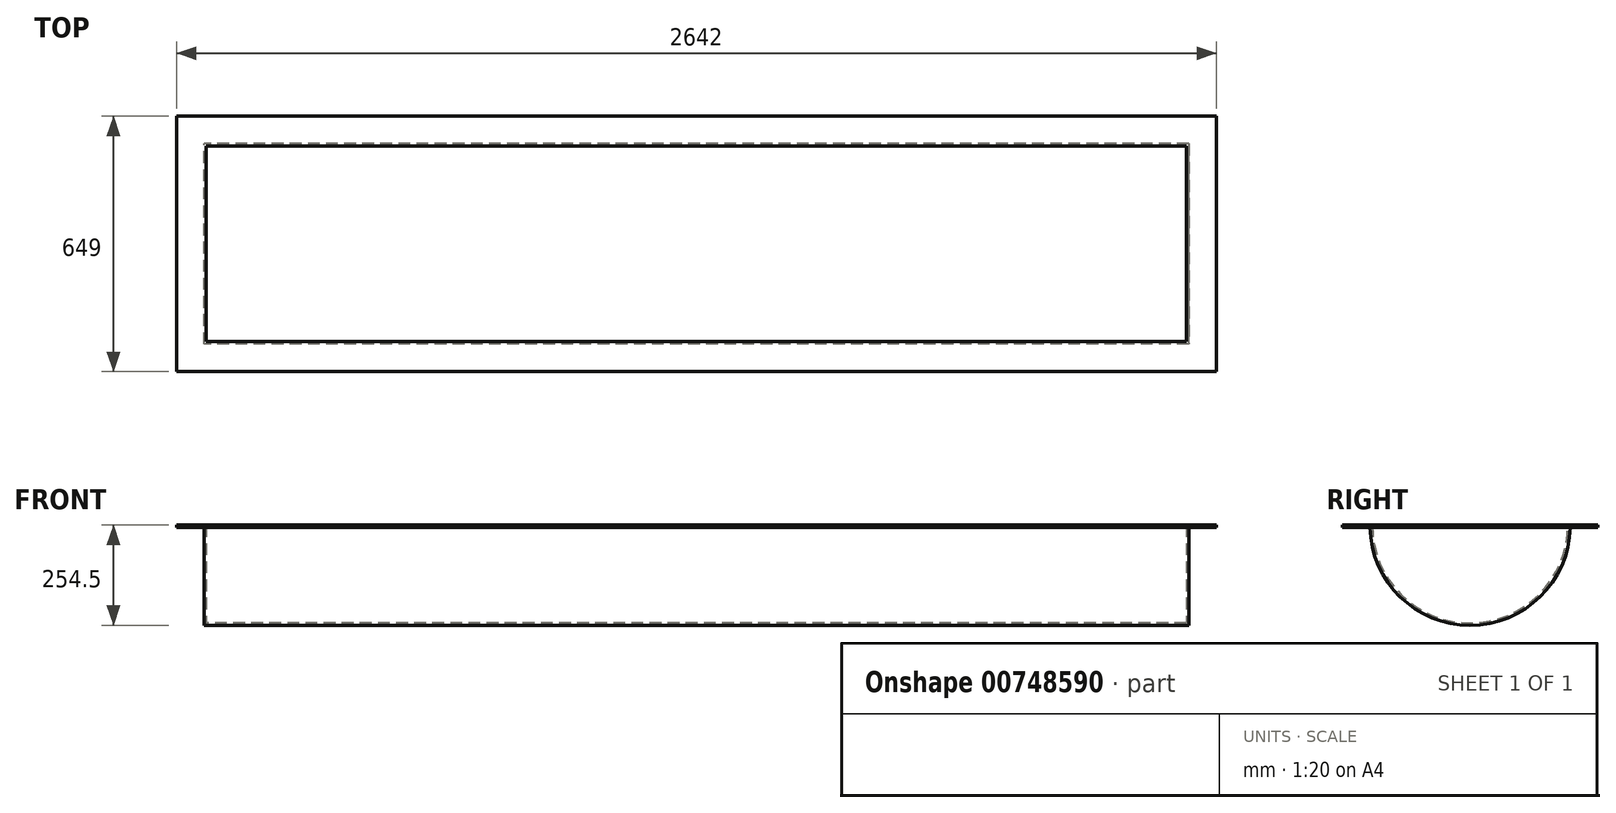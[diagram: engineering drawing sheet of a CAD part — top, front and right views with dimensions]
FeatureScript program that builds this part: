
annotation { "Feature Type Name" : "Feature", "Feature Type Description" : "" }
export const myFeature = defineFeature(function(context is Context, id is Id, definition is map)
    precondition{}
    {
        {
            var Q0;
            Q0=qCreatedBy(makeId("Right.planeOp"),FACE);
            var sketch = newSketch(context, id + "F0", { "sketchPlane" : qUnion([Q0])});
            skArc(sketch, "E0", {"start": v(-248.5, 0) * mm, "mid": v(0, -248.5) * mm, "end": v(248.5, 0) * mm});
            skArc(sketch, "E1", {"start": v(-254.5, 0) * mm, "mid": v(0, -254.5) * mm, "end": v(254.5, 0) * mm});
            skLineSegment(sketch, "E2", {"start": v(-254.5, 0) * mm, "end": v(-248.5, 0) * mm});
            skLineSegment(sketch, "E3", {"start": v(248.5, 0) * mm, "end": v(254.5, 0) * mm});
            skSolve(sketch);
        }
        {
            var Q0;
            Q0 = qSketchRegion(id + "F0", true);
            extrude(context, id + "F1", {"entities" : qUnion([Q0]), "endBound" : BoundingType.SYMMETRIC, "depth" : (2502 - 12) * mm, "offsetDistance" : 25 * mm});
        }
        {
            var Q0;
            Q0=makeQuery(id+"F1.opExtrude","CAP_FACE",FACE,{"disambiguationData":[OSD([sQuery(id+"F0.wireOp",EDGE,"E0"),sQuery(id+"F0.wireOp",EDGE,"E1"),sQuery(id+"F0.wireOp",EDGE,"E2"),sQuery(id+"F0.wireOp",EDGE,"E3")])],"isStart":false});
            var sketch = newSketch(context, id + "F2", { "sketchPlane" : qUnion([Q0])});
            skLineSegment(sketch, "E4", {"start": v(-254.5, 0) * mm, "end": v(254.5, 0) * mm});
            skArc(sketch, "E5.0", {"start": v(-254.5, 0) * mm, "mid": v(0, -254.5) * mm, "end": v(254.5, 0) * mm});
            skSolve(sketch);
        }
        {
            var Q0;
            Q0 = qSketchRegion(id + "F2", true);
            extrude(context, id + "F3", {"entities" : qUnion([Q0]), "operationType" : NewBodyOperationType.ADD, "depth" : 6 * mm, "offsetDistance" : 25 * mm});
        }
        {
            var Q0;
            Q0=makeQuery(id+"F1.opExtrude","SWEPT_BODY",BODY,{"disambiguationData":[OSD([sQuery(id+"F0.wireOp",EDGE,"E0"),sQuery(id+"F0.wireOp",EDGE,"E1"),sQuery(id+"F0.wireOp",EDGE,"E2"),sQuery(id+"F0.wireOp",EDGE,"E3")])]});
            var Q1;
            Q1=qCreatedBy(makeId("Right.planeOp"),FACE);
            mirror(context, id + "F4", {"operationType" : NewBodyOperationType.ADD, "entities" : qUnion([Q0]), "mirrorPlane" : qUnion([Q1])});
        }
        {
            var Q0;
            Q0=qCreatedBy(makeId("Top.planeOp"),FACE);
            var sketch = newSketch(context, id + "F5", { "sketchPlane" : qUnion([Q0])});
            skLineSegment(sketch, "E6.bottom", {"start": v(-1321, 324.5) * mm, "end": v(1321, 324.5) * mm});
            skLineSegment(sketch, "E6.top", {"start": v(-1321, -324.5) * mm, "end": v(1321, -324.5) * mm});
            skLineSegment(sketch, "E6.left", {"start": v(-1321, 324.5) * mm, "end": v(-1321, -324.5) * mm});
            skLineSegment(sketch, "E6.right", {"start": v(1321, 324.5) * mm, "end": v(1321, -324.5) * mm});
            skLineSegment(sketch, "E7", {"start": v(-1321, 324.5) * mm, "end": v(1321, -324.5) * mm, "construction": true});
            skSolve(sketch);
        }
        {
            var Q0;
            Q0 = qSketchRegion(id + "F5", true);
            extrude(context, id + "F6", {"entities" : qUnion([Q0]), "operationType" : NewBodyOperationType.ADD, "oppositeDirection" : true, "depth" : 6 * mm, "offsetDistance" : 25 * mm});
        }
        {
            var Q0;
            Q0=qCreatedBy(makeId("Right.planeOp"),FACE);
            var sketch = newSketch(context, id + "F7", { "sketchPlane" : qUnion([Q0])});
            skArc(sketch, "E8", {"start": v(-248.5, 0) * mm, "mid": v(0, -248.5) * mm, "end": v(248.5, 0) * mm});
            skLineSegment(sketch, "E9", {"start": v(-248.5, 0) * mm, "end": v(248.5, 0) * mm});
            skSolve(sketch);
        }
        {
            var Q0;
            Q0 = qSketchRegion(id + "F7", true);
            var Q1;
            Q1=makeQuery(id+"F4.opPattern","COPY",FACE,{"derivedFrom":makeQuery(id+"F3.opExtrude","CAP_FACE",FACE,{"disambiguationData":[OSD([sQuery(id+"F2.wireOp",EDGE,"E4"),sQuery(id+"F2.wireOp",EDGE,"E5.0")])],"isStart":true}),"instanceName":"1"});
            var Q2;
            Q2=makeQuery(id+"F3.opExtrude","CAP_FACE",FACE,{"disambiguationData":[OSD([sQuery(id+"F2.wireOp",EDGE,"E4"),sQuery(id+"F2.wireOp",EDGE,"E5.0")])],"isStart":true});
            extrude(context, id + "F8", {"entities" : qUnion([Q0]), "operationType" : NewBodyOperationType.REMOVE, "endBound" : BoundingType.UP_TO_SURFACE, "oppositeDirection" : true, "depth" : 25 * mm, "endBoundEntityFace" : qUnion([Q1]), "offsetDistance" : 25 * mm, "hasSecondDirection" : true, "secondDirectionBound" : SecondDirectionBoundingType.UP_TO_SURFACE, "secondDirectionOppositeDirection" : false, "secondDirectionDepth" : 25 * mm, "secondDirectionBoundEntityFace" : qUnion([Q2])});
        }
    });
